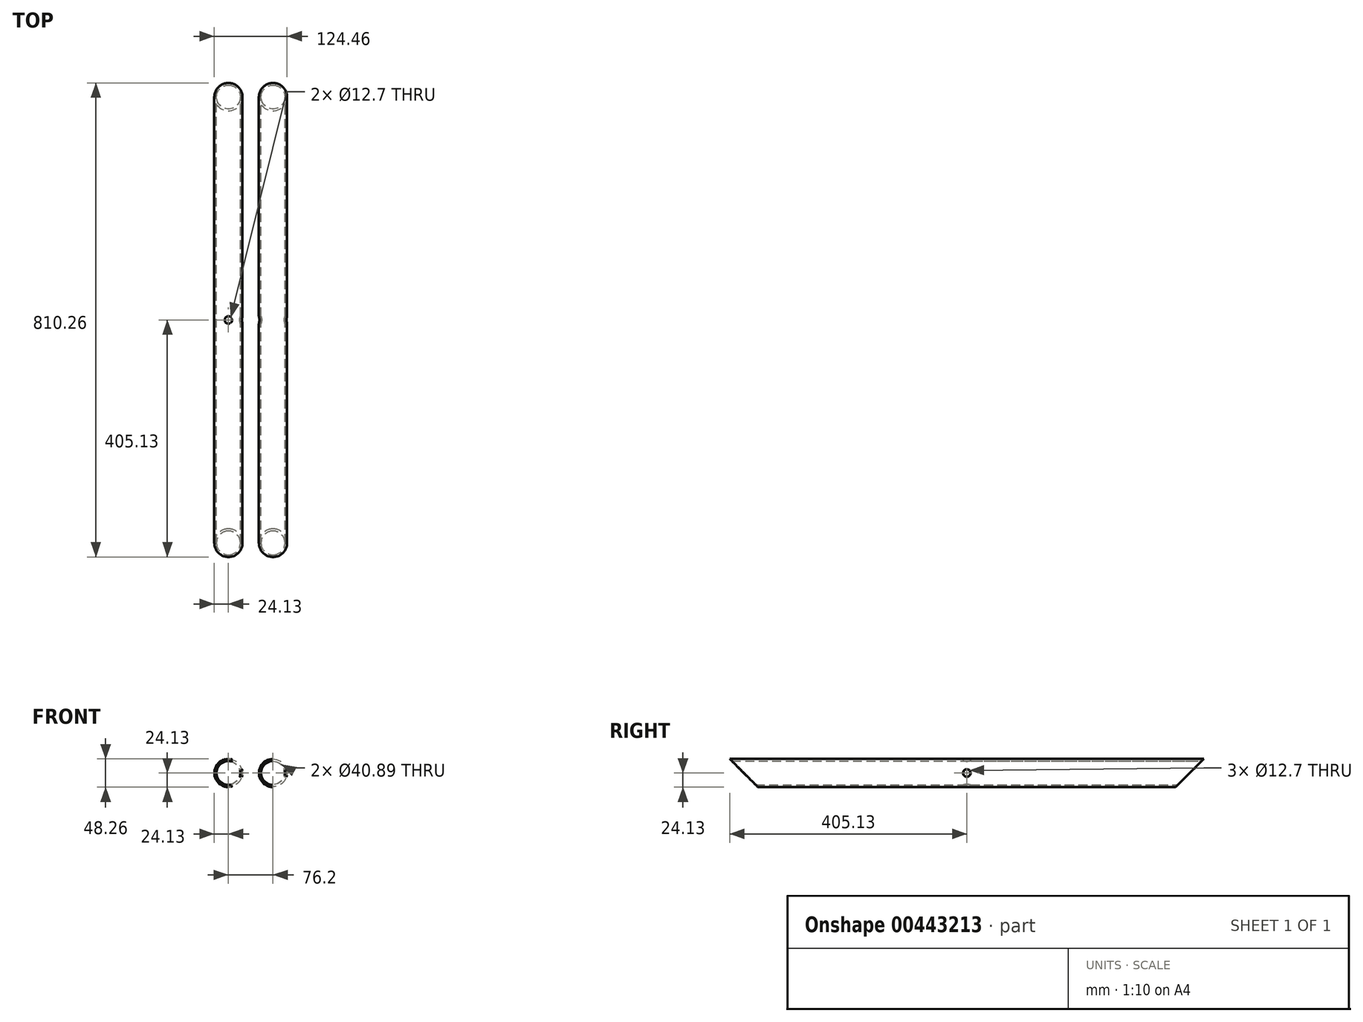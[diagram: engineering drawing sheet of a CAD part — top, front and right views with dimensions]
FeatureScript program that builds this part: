
annotation { "Feature Type Name" : "Feature", "Feature Type Description" : "" }
export const myFeature = defineFeature(function(context is Context, id is Id, definition is map)
    precondition{}
    {
        {
            var Q0;
            Q0=qCreatedBy(makeId("Front.planeOp"),FACE);
            var sketch = newSketch(context, id + "F0", { "sketchPlane" : qUnion([Q0])});
            skCircle(sketch, "E0", {"center": v(0, 0) * mm, "radius": 24.13 * mm});
            skCircle(sketch, "E1", {"center": v(0, 0) * mm, "radius": 20.45 * mm});
            skSolve(sketch);
        }
        {
            var Q0;
            Q0=makeQuery(id+"F0.imprint","IMPRINT",FACE,{"disambiguationData":[TD([[makeQuery(id+"F0.imprint","IMPRINT",EDGE,{"derivedFrom":sQuery(id+"F0.wireOp",EDGE,"E0")}),1.0]])]});
            extrude(context, id + "F1", {"entities" : qUnion([Q0]), "endBound" : BoundingType.SYMMETRIC, "depth" : 863.6 * mm});
        }
        {
            var Q0;
            Q0=qCreatedBy(makeId("Front.planeOp"),FACE);
            var sketch = newSketch(context, id + "F2", { "sketchPlane" : qUnion([Q0])});
            skCircle(sketch, "E2", {"center": v(-76.2, 0) * mm, "radius": 24.13 * mm});
            skCircle(sketch, "E3", {"center": v(-76.2, 0) * mm, "radius": 20.45 * mm});
            skSolve(sketch);
        }
        {
            var Q0;
            Q0=makeQuery(id+"F2.imprint","IMPRINT",FACE,{"disambiguationData":[TD([[makeQuery(id+"F2.imprint","IMPRINT",EDGE,{"derivedFrom":sQuery(id+"F2.wireOp",EDGE,"E2")}),1.0]])]});
            extrude(context, id + "F3", {"entities" : qUnion([Q0]), "endBound" : BoundingType.SYMMETRIC, "depth" : 914.4 * mm});
        }
        {
            var Q0;
            Q0=qCreatedBy(makeId("Right.planeOp"),FACE);
            var sketch = newSketch(context, id + "F4", { "sketchPlane" : qUnion([Q0])});
            skLineSegment(sketch, "E4", {"start": v(-463.93, 0) * mm, "end": v(464.92, 0) * mm, "construction": true});
            skLineSegment(sketch, "E5", {"start": v(-462.28, 104.5) * mm, "end": v(-486.34, -36.48) * mm});
            skLineSegment(sketch, "E6", {"start": v(-486.34, -36.48) * mm, "end": v(-324.62, -56.38) * mm});
            skLineSegment(sketch, "E7", {"start": v(-324.62, -56.38) * mm, "end": v(-381, 0) * mm});
            skLineSegment(sketch, "E8", {"start": v(-381, 0) * mm, "end": v(-424.83, 43.83) * mm});
            skLineSegment(sketch, "E9", {"start": v(-424.83, 43.83) * mm, "end": v(-462.28, 104.5) * mm});
            skLineSegment(sketch, "E10.MirrorCS", {"start": v(424.83, 43.83) * mm, "end": v(462.28, 104.5) * mm});
            skLineSegment(sketch, "E11.MirrorCS", {"start": v(462.28, 104.5) * mm, "end": v(486.34, -36.48) * mm});
            skLineSegment(sketch, "E12.MirrorCS", {"start": v(324.62, -56.38) * mm, "end": v(381, 0) * mm});
            skLineSegment(sketch, "E13.MirrorCS", {"start": v(486.34, -36.48) * mm, "end": v(324.62, -56.38) * mm});
            skLineSegment(sketch, "E14.MirrorCS", {"start": v(381, 0) * mm, "end": v(424.83, 43.83) * mm});
            skSolve(sketch);
        }
        {
            var Q0;
            Q0 = qSketchRegion(id + "F4", true);
            extrude(context, id + "F5", {"entities" : qUnion([Q0]), "operationType" : NewBodyOperationType.REMOVE, "endBound" : BoundingType.SYMMETRIC, "oppositeDirection" : true, "depth" : 304.8 * mm});
        }
        {
            var Q0;
            Q0=qCreatedBy(makeId("Right.planeOp"),FACE);
            var sketch = newSketch(context, id + "F6", { "sketchPlane" : qUnion([Q0])});
            skCircle(sketch, "E15", {"center": v(0, 0) * mm, "radius": 6.35 * mm});
            skSolve(sketch);
        }
        {
            var Q0;
            Q0 = qSketchRegion(id + "F6", true);
            extrude(context, id + "F7", {"entities" : qUnion([Q0]), "operationType" : NewBodyOperationType.REMOVE, "endBound" : BoundingType.SYMMETRIC, "oppositeDirection" : true, "depth" : 152.4 * mm});
        }
        {
            var Q0;
            Q0=qCreatedBy(makeId("Top.planeOp"),FACE);
            var sketch = newSketch(context, id + "F8", { "sketchPlane" : qUnion([Q0])});
            skCircle(sketch, "E16", {"center": v(-76.2, 0) * mm, "radius": 6.35 * mm});
            skSolve(sketch);
        }
        {
            var Q0;
            Q0 = qSketchRegion(id + "F8", true);
            extrude(context, id + "F9", {"entities" : qUnion([Q0]), "operationType" : NewBodyOperationType.REMOVE, "endBound" : BoundingType.SYMMETRIC, "depth" : 152.4 * mm});
        }
    });
